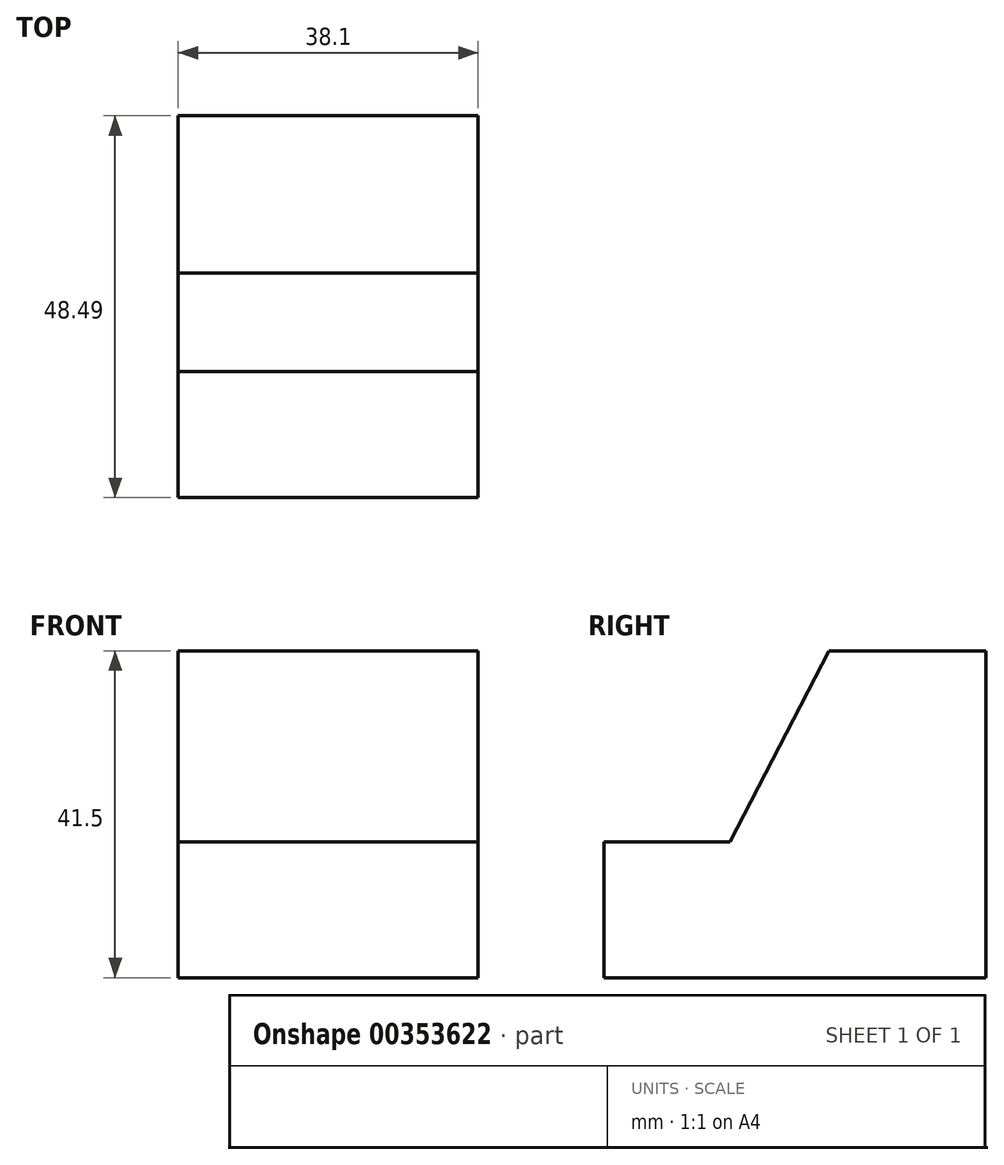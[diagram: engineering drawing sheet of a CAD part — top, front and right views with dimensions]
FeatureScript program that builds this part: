
annotation { "Feature Type Name" : "Feature", "Feature Type Description" : "" }
export const myFeature = defineFeature(function(context is Context, id is Id, definition is map)
    precondition{}
    {
        {
            var Q0;
            Q0=qCreatedBy(makeId("Right.planeOp"),FACE);
            var sketch = newSketch(context, id + "F0", { "sketchPlane" : qUnion([Q0])});
            skLineSegment(sketch, "E0", {"start": v(0, 0) * mm, "end": v(0, 41.5) * mm});
            skLineSegment(sketch, "E1", {"start": v(0, 41.5) * mm, "end": v(-19.97, 41.5) * mm});
            skLineSegment(sketch, "E2", {"start": v(-19.97, 41.5) * mm, "end": v(-32.52, 17.26) * mm});
            skLineSegment(sketch, "E3", {"start": v(-32.52, 17.26) * mm, "end": v(-48.5, 17.26) * mm});
            skLineSegment(sketch, "E4", {"start": v(-48.5, 17.26) * mm, "end": v(-48.5, 0) * mm});
            skLineSegment(sketch, "E5", {"start": v(-48.5, 0) * mm, "end": v(0, 0) * mm});
            skSolve(sketch);
        }
        {
            var Q0;
            Q0 = qSketchRegion(id + "F0", true);
            extrude(context, id + "F1", {"entities" : qUnion([Q0]), "depth" : 38.1 * mm});
        }
    });
